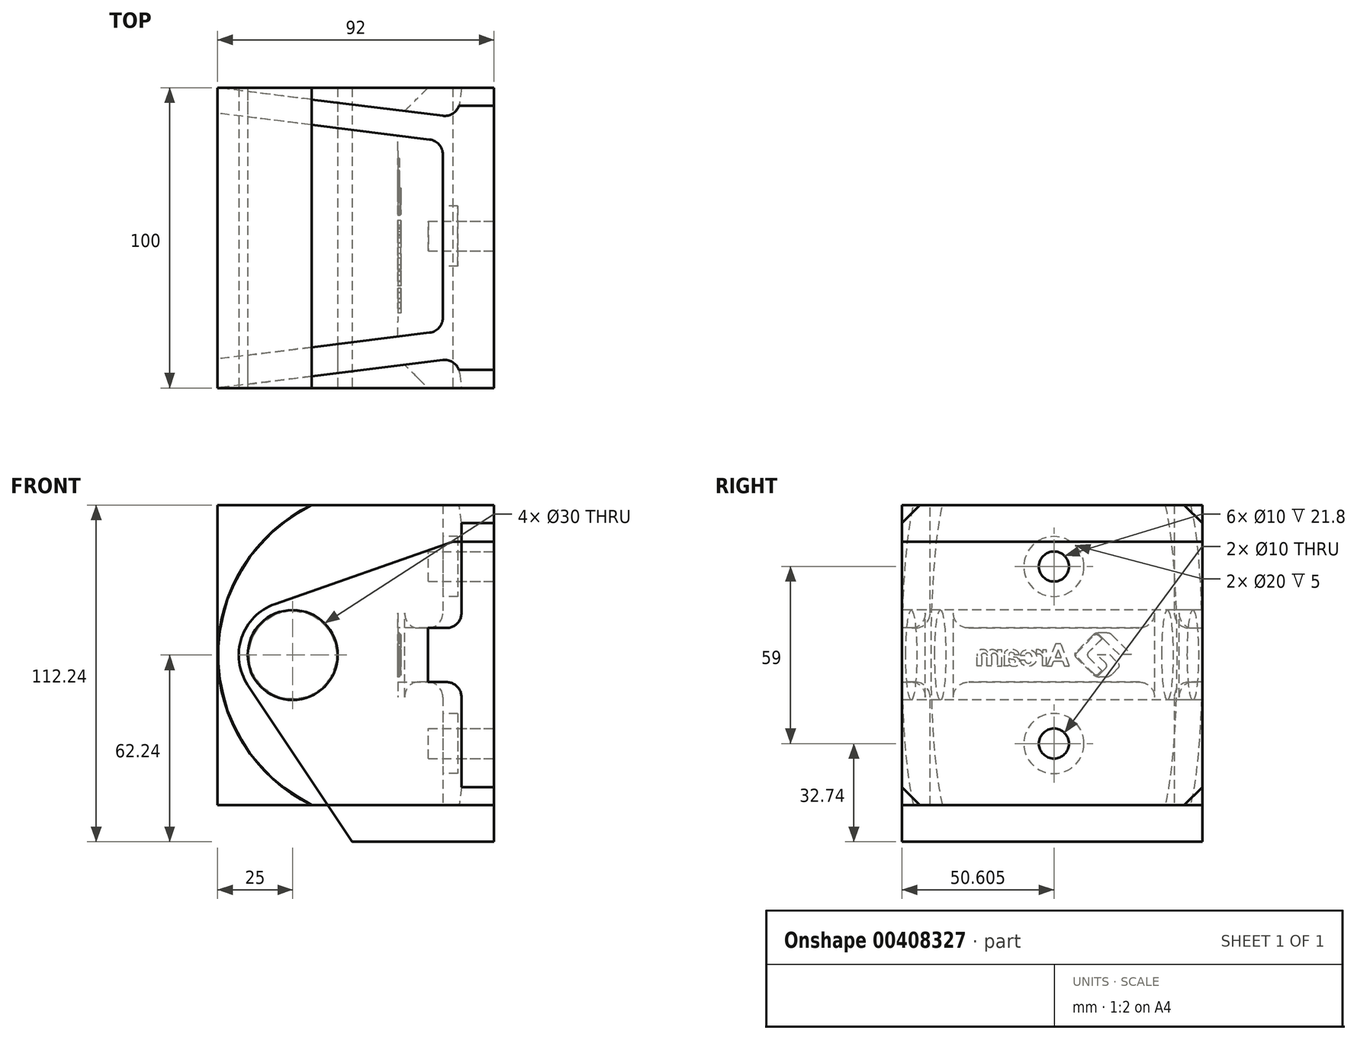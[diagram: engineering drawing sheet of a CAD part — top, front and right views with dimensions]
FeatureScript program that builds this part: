
annotation { "Feature Type Name" : "Feature", "Feature Type Description" : "" }
export const myFeature = defineFeature(function(context is Context, id is Id, definition is map)
    precondition{}
    {
        {
            assignVariable(context, id + "F0", {"name" : "length", "anyValue" : 100});
        }
        {
            assignVariable(context, id + "F1", {"name" : "thickness", "anyValue" : 12});
        }
        {
            var Q0;
            Q0=qCreatedBy(makeId("Top.planeOp"),FACE);
            var sketch = newSketch(context, id + "F2", { "sketchPlane" : qUnion([Q0])});
            skLineSegment(sketch, "E0", {"start": v(0, 0) * mm, "end": v(0, 100) * mm});
            skLineSegment(sketch, "E1", {"start": v(-92, 9.67) * mm, "end": v(-92, 0) * mm});
            skLineSegment(sketch, "E2", {"start": v(-92, 0) * mm, "end": v(-12.03, 9.92) * mm});
            skLineSegment(sketch, "E3", {"start": v(-12.03, 90.08) * mm, "end": v(-92, 100) * mm});
            skLineSegment(sketch, "E4", {"start": v(-92, 100) * mm, "end": v(-92, 91.54) * mm});
            skLineSegment(sketch, "E5", {"start": v(-92, 9.67) * mm, "end": v(-17, 18.98) * mm});
            skLineSegment(sketch, "E6", {"start": v(-17, 82.23) * mm, "end": v(-92, 91.54) * mm});
            skLineSegment(sketch, "E7", {"start": v(-10.8, 0) * mm, "end": v(0, 0) * mm});
            skLineSegment(sketch, "E8", {"start": v(-10.8, 100) * mm, "end": v(0, 100) * mm});
            skLineSegment(sketch, "E9", {"start": v(-12.03, 9.92) * mm, "end": v(-10.8, 0) * mm});
            skLineSegment(sketch, "E10", {"start": v(-17, 18.98) * mm, "end": v(-17, 82.23) * mm});
            skLineSegment(sketch, "E11", {"start": v(-12.03, 90.08) * mm, "end": v(-10.8, 100) * mm});
            skSolve(sketch);
        }
        {
            var Q0;
            Q0=makeQuery(id+"F2.imprint","IMPRINT",FACE,{"disambiguationData":[TD([[makeQuery(id+"F2.imprint","IMPRINT",EDGE,{"derivedFrom":sQuery(id+"F2.wireOp",EDGE,"E0")}),1.0]])]});
            extrude(context, id + "F3", {"entities" : qUnion([Q0]), "endBound" : BoundingType.SYMMETRIC, "depth" : 100 * mm});
        }
        {
            var Q0;
            Q0=qCreatedBy(makeId("Front.planeOp"),FACE);
            var sketch = newSketch(context, id + "F4", { "sketchPlane" : qUnion([Q0])});
            skLineSegment(sketch, "E12", {"start": v(-117, 60) * mm, "end": v(-117, -60) * mm});
            skLineSegment(sketch, "E13", {"start": v(-117, -60) * mm, "end": v(-47, -60) * mm});
            skLineSegment(sketch, "E14", {"start": v(-47, -60) * mm, "end": v(-107, 0) * mm});
            skLineSegment(sketch, "E15", {"start": v(-107, 0) * mm, "end": v(-47, 60) * mm});
            skLineSegment(sketch, "E16", {"start": v(-47, 60) * mm, "end": v(-117, 60) * mm});
            skArc(sketch, "E17", {"start": v(-12.03, 50) * mm, "mid": v(-92, 0) * mm, "end": v(-12.03, -50) * mm});
            skPoint(sketch, "E17.first.point", {"position": v(-12.03, 50) * mm});
            skPoint(sketch, "E17.second.point", {"position": v(-92, 0) * mm});
            skPoint(sketch, "E17.third.point", {"position": v(-12.03, -50) * mm});
            skLineSegment(sketch, "E18", {"start": v(-12.03, 50) * mm, "end": v(-12.03, -50) * mm});
            skArc(sketch, "E19.0", {"start": v(-12.03, 76.85) * mm, "mid": v(-117, 0) * mm, "end": v(-12.03, -76.85) * mm});
            skLineSegment(sketch, "E20", {"start": v(-12.03, 50) * mm, "end": v(-12.03, 76.85) * mm});
            skLineSegment(sketch, "E21", {"start": v(-12.03, -50) * mm, "end": v(-12.03, -76.85) * mm});
            skSolve(sketch);
        }
        {
            var Q0;
            {var subQ1=sQuery(id+"F4.wireOp",EDGE,"E14");var subQ6=sQuery(id+"F4.wireOp",EDGE,"E13");var subQ7=makeQuery(id+"F4.imprint","INTERSECT",VERTEX,{"derivedFrom":[subQ6,subQ1]});Q0=makeQuery(id+"F4.imprint","IMPRINT",FACE,{"disambiguationData":[TD([[makeQuery(id+"F4.imprint","IMPRINT",EDGE,{"disambiguationData":[TD([[subQ7,1.0]])],"derivedFrom":subQ6}),1.0]])]});}
            var Q1;
            {var subQ0=sQuery(id+"F4.wireOp",EDGE,"E15");var subQ1=sQuery(id+"F4.wireOp",EDGE,"E14");var subQ2=makeQuery(id+"F4.imprint","INTERSECT",VERTEX,{"derivedFrom":[subQ1,subQ0]});Q1=makeQuery(id+"F4.imprint","IMPRINT",FACE,{"disambiguationData":[TD([[makeQuery(id+"F4.imprint","IMPRINT",EDGE,{"disambiguationData":[TD([[subQ2,1.0]])],"derivedFrom":subQ1}),-1.0]])]});}
            var Q2;
            Q2 = qConstructionFilter(qBodyType(qCreatedBy(id + "F4" ,EDGE), BodyType.WIRE), ConstructionObject.NO);
            extrude(context, id + "F5", {"entities" : qUnion([Q0, Q1]), "operationType" : NewBodyOperationType.REMOVE, "surfaceEntities" : qUnion([Q2]), "oppositeDirection" : true, "depth" : 111.8 * mm});
        }
        {
            var Q0;
            Q0=qCreatedBy(makeId("Front.planeOp"),FACE);
            var sketch = newSketch(context, id + "F6", { "sketchPlane" : qUnion([Q0])});
            skCircle(sketch, "E22", {"center": v(-67, 0) * mm, "radius": 15 * mm});
            skSolve(sketch);
        }
        {
            var Q0;
            Q0 = qSketchRegion(id + "F6", true);
            var Q1;
            Q1=sQuery(id+"F6.wireOp",EDGE,"E22");
            extrude(context, id + "F7", {"entities" : qUnion([Q0]), "operationType" : NewBodyOperationType.REMOVE, "surfaceEntities" : qUnion([Q1]), "oppositeDirection" : true, "depth" : 108 * mm});
        }
        {
            var Q0;
            Q0=qCreatedBy(makeId("Front.planeOp"),FACE);
            var sketch = newSketch(context, id + "F8", { "sketchPlane" : qUnion([Q0])});
            skLineSegment(sketch, "E23.bottom", {"start": v(0, -9) * mm, "end": v(-32, -9) * mm});
            skLineSegment(sketch, "E23.top", {"start": v(0, 9) * mm, "end": v(-32, 9) * mm});
            skLineSegment(sketch, "E23.left", {"start": v(-32, 9) * mm, "end": v(-32, -9) * mm});
            skLineSegment(sketch, "E23.right", {"start": v(0, 9) * mm, "end": v(0, -9) * mm});
            skSolve(sketch);
        }
        {
            var Q0;
            Q0 = qSketchRegion(id + "F8", true);
            extrude(context, id + "F9", {"entities" : qUnion([Q0]), "operationType" : NewBodyOperationType.ADD, "oppositeDirection" : true, "depth" : (getVariable(context, 'length')) * mm});
        }
        {
            var Q0;
            Q0=makeQuery(id+"F3.opExtrude","CAP_EDGE",EDGE,{"disambiguationData":[OSD([sQuery(id+"F2.wireOp",EDGE,"vjMEqo8n-QfoI-5M5s-0d4p-3gr9z9UQkxS1")])],"isStart":true});
            var Q1;
            Q1=makeQuery(id+"F3.opExtrude","CAP_EDGE",EDGE,{"disambiguationData":[OSD([sQuery(id+"F2.wireOp",EDGE,"vjMEqo8n-QfoI-5M5s-0d4p-3gr9z9UQkxS1")])],"isStart":false});
            var Q2;
            Q2=makeQuery(id+"F3.opExtrude","CAP_EDGE",EDGE,{"disambiguationData":[OSD([sQuery(id+"F2.wireOp",EDGE,"uyNWYaNW-0dKr-tjX5-kQlW-Z3eX3tDSU0gN")])],"isStart":true});
            var Q3;
            Q3=makeQuery(id+"F3.opExtrude","CAP_EDGE",EDGE,{"disambiguationData":[OSD([sQuery(id+"F2.wireOp",EDGE,"uyNWYaNW-0dKr-tjX5-kQlW-Z3eX3tDSU0gN")])],"isStart":false});
            var Q4;
            Q4=makeQuery(id+"F3.opExtrude","CAP_EDGE",EDGE,{"disambiguationData":[OSD([sQuery(id+"F2.wireOp",EDGE,"E8")])],"isStart":false});
            var Q5;
            Q5=makeQuery(id+"F3.opExtrude","CAP_EDGE",EDGE,{"disambiguationData":[OSD([sQuery(id+"F2.wireOp",EDGE,"E8")])],"isStart":true});
            var Q6;
            Q6=makeQuery(id+"F3.opExtrude","CAP_EDGE",EDGE,{"disambiguationData":[OSD([sQuery(id+"F2.wireOp",EDGE,"E7")])],"isStart":true});
            var Q7;
            Q7=makeQuery(id+"F3.opExtrude","CAP_EDGE",EDGE,{"disambiguationData":[OSD([sQuery(id+"F2.wireOp",EDGE,"E7")])],"isStart":false});
            chamfer(context, id + "F10", {"entities" : qUnion([Q0, Q1, Q2, Q3, Q4, Q5, Q6, Q7]), "width" : 6 * mm, "tangentPropagation" : true});
        }
        {
            var Q0;
            Q0=qCreatedBy(makeId("Right.planeOp"),FACE);
            var sketch = newSketch(context, id + "F11", { "sketchPlane" : qUnion([Q0])});
            skCircle(sketch, "E24", {"center": v(50.6, 29.5) * mm, "radius": 5 * mm});
            skCircle(sketch, "E25.MirrorC", {"center": v(50.6, -29.5) * mm, "radius": 5 * mm});
            skLineSegment(sketch, "E26.direction1", {"start": v(50.6, 29.5) * mm, "end": v(19.52, 29.5) * mm, "construction": true});
            skLineSegment(sketch, "E27", {"start": v(82.23, 29.5) * mm, "end": v(18.98, 29.5) * mm});
            skLineSegment(sketch, "E28", {"start": v(50.6, 50) * mm, "end": v(50.6, 9) * mm});
            skSolve(sketch);
        }
        {
            var Q0;
            Q0 = qSketchRegion(id + "F11", true);
            extrude(context, id + "F12", {"entities" : qUnion([Q0]), "operationType" : NewBodyOperationType.REMOVE, "endBound" : BoundingType.UP_TO_NEXT, "oppositeDirection" : true, "depth" : (getVariable(context, 'thickness')) * mm});
        }
        {
            var Q0;
            {var subQ0=sQuery(id+"F2.wireOp",EDGE,"E10");Q0=makeQuery(id+"F9.boolean.opBoolean","SPLIT",FACE,{"disambiguationData":[TD([makeQuery(id+"F9.opExtrude","SWEPT_FACE",FACE,{"disambiguationData":[OSD([sQuery(id+"F8.wireOp",EDGE,"E23.bottom")])]})])],"derivedFrom":makeQuery(id+"F3.opExtrude","SWEPT_FACE",FACE,{"disambiguationData":[OSD([subQ0])]})});}
            cPlane(context, id + "F13", {"entities" : qUnion([Q0]), "cplaneType" : CPlaneType.OFFSET, "offset" : 0 * mm, "width" : 150 * mm, "height" : 150 * mm});
        }
        {
            var Q0;
            Q0=qCreatedBy(id+"F13.planeOp",FACE);
            var sketch = newSketch(context, id + "F14", { "sketchPlane" : qUnion([Q0])});
            skCircle(sketch, "E29.0", {"center": v(-50.6, 29.5) * mm, "radius": 10 * mm});
            skCircle(sketch, "E30.0", {"center": v(-50.6, -29.5) * mm, "radius": 10 * mm});
            skSolve(sketch);
        }
        {
            var Q0;
            Q0 = qSketchRegion(id + "F14", true);
            extrude(context, id + "F15", {"entities" : qUnion([Q0]), "operationType" : NewBodyOperationType.REMOVE, "oppositeDirection" : true, "depth" : 5 * mm});
        }
        {
            assignVariable(context, id + "F16", {"name" : "millradius", "anyValue" : 5});
        }
        {
            var Q0;
            Q0=makeQuery(id+"F9.boolean.opBoolean","INTERSECT",EDGE,{"derivedFrom":[makeQuery(id+"F3.opExtrude","SWEPT_FACE",FACE,{"disambiguationData":[OSD([sQuery(id+"F2.wireOp",EDGE,"E9")])]}),makeQuery(id+"F9.opExtrude","SWEPT_FACE",FACE,{"disambiguationData":[OSD([sQuery(id+"F8.wireOp",EDGE,"E23.top")])]})]});
            var Q1;
            Q1=makeQuery(id+"F9.boolean.opBoolean","INTERSECT",EDGE,{"derivedFrom":[makeQuery(id+"F3.opExtrude","SWEPT_FACE",FACE,{"disambiguationData":[OSD([sQuery(id+"F2.wireOp",EDGE,"E2")])]}),makeQuery(id+"F9.opExtrude","SWEPT_FACE",FACE,{"disambiguationData":[OSD([sQuery(id+"F8.wireOp",EDGE,"E23.top")])]})]});
            var Q2;
            {var subQ0=sQuery(id+"F2.wireOp",EDGE,"E9");var subQ1=sQuery(id+"F2.wireOp",EDGE,"E2");Q2=makeQuery(id+"F9.boolean.opBoolean","SPLIT",EDGE,{"disambiguationData":[TD([makeQuery(id+"F9.opExtrude","SWEPT_FACE",FACE,{"disambiguationData":[OSD([sQuery(id+"F8.wireOp",EDGE,"E23.top")])]})])],"derivedFrom":makeQuery(id+"F3.opExtrude","SWEPT_EDGE",EDGE,{"disambiguationData":[OSD([subQ1,subQ0])]})});}
            var Q3;
            Q3=makeQuery(id+"F9.boolean.opBoolean","INTERSECT",EDGE,{"derivedFrom":[makeQuery(id+"F3.opExtrude","SWEPT_FACE",FACE,{"disambiguationData":[OSD([sQuery(id+"F2.wireOp",EDGE,"E2")])]}),makeQuery(id+"F9.opExtrude","SWEPT_FACE",FACE,{"disambiguationData":[OSD([sQuery(id+"F8.wireOp",EDGE,"E23.bottom")])]})]});
            var Q4;
            Q4=makeQuery(id+"F9.boolean.opBoolean","INTERSECT",EDGE,{"derivedFrom":[makeQuery(id+"F3.opExtrude","SWEPT_FACE",FACE,{"disambiguationData":[OSD([sQuery(id+"F2.wireOp",EDGE,"E9")])]}),makeQuery(id+"F9.opExtrude","SWEPT_FACE",FACE,{"disambiguationData":[OSD([sQuery(id+"F8.wireOp",EDGE,"E23.bottom")])]})]});
            var Q5;
            {var subQ0=sQuery(id+"F2.wireOp",EDGE,"E9");var subQ1=sQuery(id+"F2.wireOp",EDGE,"E2");Q5=makeQuery(id+"F9.boolean.opBoolean","SPLIT",EDGE,{"disambiguationData":[TD([makeQuery(id+"F9.opExtrude","SWEPT_FACE",FACE,{"disambiguationData":[OSD([sQuery(id+"F8.wireOp",EDGE,"E23.bottom")])]})])],"derivedFrom":makeQuery(id+"F3.opExtrude","SWEPT_EDGE",EDGE,{"disambiguationData":[OSD([subQ1,subQ0])]})});}
            var Q6;
            {var subQ0=sQuery(id+"F2.wireOp",EDGE,"E10");var subQ1=sQuery(id+"F2.wireOp",EDGE,"E5");Q6=makeQuery(id+"F9.boolean.opBoolean","SPLIT",EDGE,{"disambiguationData":[TD([makeQuery(id+"F9.opExtrude","SWEPT_FACE",FACE,{"disambiguationData":[OSD([sQuery(id+"F8.wireOp",EDGE,"E23.top")])]})])],"derivedFrom":makeQuery(id+"F3.opExtrude","SWEPT_EDGE",EDGE,{"disambiguationData":[OSD([subQ1,subQ0])]})});}
            var Q7;
            Q7=makeQuery(id+"F9.boolean.opBoolean","INTERSECT",EDGE,{"derivedFrom":[makeQuery(id+"F3.opExtrude","SWEPT_FACE",FACE,{"disambiguationData":[OSD([sQuery(id+"F2.wireOp",EDGE,"E5")])]}),makeQuery(id+"F9.opExtrude","SWEPT_FACE",FACE,{"disambiguationData":[OSD([sQuery(id+"F8.wireOp",EDGE,"E23.top")])]})]});
            var Q8;
            Q8=makeQuery(id+"F9.boolean.opBoolean","INTERSECT",EDGE,{"derivedFrom":[makeQuery(id+"F3.opExtrude","SWEPT_FACE",FACE,{"disambiguationData":[OSD([sQuery(id+"F2.wireOp",EDGE,"E10")])]}),makeQuery(id+"F9.opExtrude","SWEPT_FACE",FACE,{"disambiguationData":[OSD([sQuery(id+"F8.wireOp",EDGE,"E23.top")])]})]});
            var Q9;
            Q9=makeQuery(id+"F9.boolean.opBoolean","INTERSECT",EDGE,{"derivedFrom":[makeQuery(id+"F3.opExtrude","SWEPT_FACE",FACE,{"disambiguationData":[OSD([sQuery(id+"F2.wireOp",EDGE,"E6")])]}),makeQuery(id+"F9.opExtrude","SWEPT_FACE",FACE,{"disambiguationData":[OSD([sQuery(id+"F8.wireOp",EDGE,"E23.top")])]})]});
            var Q10;
            {var subQ0=sQuery(id+"F2.wireOp",EDGE,"E10");var subQ1=sQuery(id+"F2.wireOp",EDGE,"E6");Q10=makeQuery(id+"F9.boolean.opBoolean","SPLIT",EDGE,{"disambiguationData":[TD([makeQuery(id+"F9.opExtrude","SWEPT_FACE",FACE,{"disambiguationData":[OSD([sQuery(id+"F8.wireOp",EDGE,"E23.top")])]})])],"derivedFrom":makeQuery(id+"F3.opExtrude","SWEPT_EDGE",EDGE,{"disambiguationData":[OSD([subQ1,subQ0])]})});}
            var Q11;
            {var subQ0=sQuery(id+"F2.wireOp",EDGE,"E10");var subQ1=sQuery(id+"F2.wireOp",EDGE,"E6");Q11=makeQuery(id+"F9.boolean.opBoolean","SPLIT",EDGE,{"disambiguationData":[TD([makeQuery(id+"F9.opExtrude","SWEPT_FACE",FACE,{"disambiguationData":[OSD([sQuery(id+"F8.wireOp",EDGE,"E23.bottom")])]})])],"derivedFrom":makeQuery(id+"F3.opExtrude","SWEPT_EDGE",EDGE,{"disambiguationData":[OSD([subQ1,subQ0])]})});}
            var Q12;
            Q12=makeQuery(id+"F9.boolean.opBoolean","INTERSECT",EDGE,{"derivedFrom":[makeQuery(id+"F3.opExtrude","SWEPT_FACE",FACE,{"disambiguationData":[OSD([sQuery(id+"F2.wireOp",EDGE,"E6")])]}),makeQuery(id+"F9.opExtrude","SWEPT_FACE",FACE,{"disambiguationData":[OSD([sQuery(id+"F8.wireOp",EDGE,"E23.bottom")])]})]});
            var Q13;
            Q13=makeQuery(id+"F9.boolean.opBoolean","INTERSECT",EDGE,{"derivedFrom":[makeQuery(id+"F3.opExtrude","SWEPT_FACE",FACE,{"disambiguationData":[OSD([sQuery(id+"F2.wireOp",EDGE,"E10")])]}),makeQuery(id+"F9.opExtrude","SWEPT_FACE",FACE,{"disambiguationData":[OSD([sQuery(id+"F8.wireOp",EDGE,"E23.bottom")])]})]});
            var Q14;
            Q14=makeQuery(id+"F9.boolean.opBoolean","INTERSECT",EDGE,{"derivedFrom":[makeQuery(id+"F3.opExtrude","SWEPT_FACE",FACE,{"disambiguationData":[OSD([sQuery(id+"F2.wireOp",EDGE,"E5")])]}),makeQuery(id+"F9.opExtrude","SWEPT_FACE",FACE,{"disambiguationData":[OSD([sQuery(id+"F8.wireOp",EDGE,"E23.bottom")])]})]});
            var Q15;
            {var subQ0=sQuery(id+"F2.wireOp",EDGE,"E10");var subQ1=sQuery(id+"F2.wireOp",EDGE,"E5");Q15=makeQuery(id+"F9.boolean.opBoolean","SPLIT",EDGE,{"disambiguationData":[TD([makeQuery(id+"F9.opExtrude","SWEPT_FACE",FACE,{"disambiguationData":[OSD([sQuery(id+"F8.wireOp",EDGE,"E23.bottom")])]})])],"derivedFrom":makeQuery(id+"F3.opExtrude","SWEPT_EDGE",EDGE,{"disambiguationData":[OSD([subQ1,subQ0])]})});}
            var Q16;
            Q16=makeQuery(id+"F9.boolean.opBoolean","INTERSECT",EDGE,{"derivedFrom":[makeQuery(id+"F3.opExtrude","SWEPT_FACE",FACE,{"disambiguationData":[OSD([sQuery(id+"F2.wireOp",EDGE,"E3")])]}),makeQuery(id+"F9.opExtrude","SWEPT_FACE",FACE,{"disambiguationData":[OSD([sQuery(id+"F8.wireOp",EDGE,"E23.bottom")])]})]});
            var Q17;
            Q17=makeQuery(id+"F9.boolean.opBoolean","INTERSECT",EDGE,{"derivedFrom":[makeQuery(id+"F3.opExtrude","SWEPT_FACE",FACE,{"disambiguationData":[OSD([sQuery(id+"F2.wireOp",EDGE,"E11")])]}),makeQuery(id+"F9.opExtrude","SWEPT_FACE",FACE,{"disambiguationData":[OSD([sQuery(id+"F8.wireOp",EDGE,"E23.bottom")])]})]});
            var Q18;
            {var subQ0=sQuery(id+"F2.wireOp",EDGE,"E11");var subQ1=sQuery(id+"F2.wireOp",EDGE,"E3");Q18=makeQuery(id+"F9.boolean.opBoolean","SPLIT",EDGE,{"disambiguationData":[TD([makeQuery(id+"F9.opExtrude","SWEPT_FACE",FACE,{"disambiguationData":[OSD([sQuery(id+"F8.wireOp",EDGE,"E23.bottom")])]})])],"derivedFrom":makeQuery(id+"F3.opExtrude","SWEPT_EDGE",EDGE,{"disambiguationData":[OSD([subQ1,subQ0])]})});}
            var Q19;
            Q19=makeQuery(id+"F9.boolean.opBoolean","INTERSECT",EDGE,{"derivedFrom":[makeQuery(id+"F3.opExtrude","SWEPT_FACE",FACE,{"disambiguationData":[OSD([sQuery(id+"F2.wireOp",EDGE,"E3")])]}),makeQuery(id+"F9.opExtrude","SWEPT_FACE",FACE,{"disambiguationData":[OSD([sQuery(id+"F8.wireOp",EDGE,"E23.top")])]})]});
            var Q20;
            Q20=makeQuery(id+"F9.boolean.opBoolean","INTERSECT",EDGE,{"derivedFrom":[makeQuery(id+"F3.opExtrude","SWEPT_FACE",FACE,{"disambiguationData":[OSD([sQuery(id+"F2.wireOp",EDGE,"E11")])]}),makeQuery(id+"F9.opExtrude","SWEPT_FACE",FACE,{"disambiguationData":[OSD([sQuery(id+"F8.wireOp",EDGE,"E23.top")])]})]});
            var Q21;
            {var subQ0=sQuery(id+"F2.wireOp",EDGE,"E11");var subQ1=sQuery(id+"F2.wireOp",EDGE,"E3");Q21=makeQuery(id+"F9.boolean.opBoolean","SPLIT",EDGE,{"disambiguationData":[TD([makeQuery(id+"F9.opExtrude","SWEPT_FACE",FACE,{"disambiguationData":[OSD([sQuery(id+"F8.wireOp",EDGE,"E23.top")])]})])],"derivedFrom":makeQuery(id+"F3.opExtrude","SWEPT_EDGE",EDGE,{"disambiguationData":[OSD([subQ1,subQ0])]})});}
            fillet(context, id + "F17", {"entities" : qUnion([Q0, Q1, Q2, Q3, Q4, Q5, Q6, Q7, Q8, Q9, Q10, Q11, Q12, Q13, Q14, Q15, Q16, Q17, Q18, Q19, Q20, Q21]), "radius" : (getVariable(context, 'millradius')) * mm, "tangentPropagation" : true, "allowEdgeOverflow" : false});
        }
        {
            var Q0;
            Q0=makeQuery(id+"F9.opExtrude","CAP_EDGE",EDGE,{"disambiguationData":[OSD([sQuery(id+"F8.wireOp",EDGE,"E23.left")])],"isStart":true});
            var Q1;
            Q1=makeQuery(id+"F9.opExtrude","CAP_EDGE",EDGE,{"disambiguationData":[OSD([sQuery(id+"F8.wireOp",EDGE,"E23.left")])],"isStart":false});
            chamfer(context, id + "F18", {"entities" : qUnion([Q0, Q1]), "width" : 10 * mm, "tangentPropagation" : true});
        }
        {
            var Q0;
            Q0=qCreatedBy(makeId("Top.planeOp"),FACE);
            var sketch = newSketch(context, id + "F19", { "sketchPlane" : qUnion([Q0])});
            skLineSegment(sketch, "E31.bottom", {"start": v(0, 0) * mm, "end": v(-92, 0) * mm});
            skLineSegment(sketch, "E31.top", {"start": v(0, 100) * mm, "end": v(-92, 100) * mm});
            skLineSegment(sketch, "E31.left", {"start": v(0, 0) * mm, "end": v(0, 100) * mm});
            skLineSegment(sketch, "E31.right", {"start": v(-92, 0) * mm, "end": v(-92, 100) * mm});
            skSolve(sketch);
        }
        {
            var Q0;
            Q0 = qSketchRegion(id + "F19", true);
            extrude(context, id + "F20", {"entities" : qUnion([Q0]), "endBound" : BoundingType.SYMMETRIC, "depth" : (getVariable(context, 'length')) * mm});
        }
        {
            var Q0;
            Q0=makeQuery(id+"F9.boolean.opBoolean","MERGE",FACE,{"derivedFrom":[makeQuery(id+"F3.opExtrude","SWEPT_FACE",FACE,{"disambiguationData":[OSD([sQuery(id+"F2.wireOp",EDGE,"E7")])]}),makeQuery(id+"F9.opExtrude","CAP_FACE",FACE,{"disambiguationData":[OSD([sQuery(id+"F8.wireOp",EDGE,"E23.bottom"),sQuery(id+"F8.wireOp",EDGE,"E23.top"),sQuery(id+"F8.wireOp",EDGE,"E23.left"),sQuery(id+"F8.wireOp",EDGE,"E23.right")])],"isStart":true})]});
            cPlane(context, id + "F21", {"entities" : qUnion([Q0]), "cplaneType" : CPlaneType.OFFSET, "offset" : 0 * mm, "width" : 150 * mm, "height" : 150 * mm});
        }
        {
            var Q0;
            Q0=qCreatedBy(id+"F21.planeOp",FACE);
            var sketch = newSketch(context, id + "F22", { "sketchPlane" : qUnion([Q0])});
            skLineSegment(sketch, "E32.0", {"start": v(-60.74, -50) * mm, "end": v(-17, -50) * mm});
            skLineSegment(sketch, "E32.1", {"start": v(-11.66, -50) * mm, "end": v(-17, -50) * mm});
            skArc(sketch, "E32.2", {"start": v(-60.74, -50) * mm, "mid": v(-92, 0) * mm, "end": v(-60.74, 50) * mm});
            skLineSegment(sketch, "E32.3", {"start": v(0, -50) * mm, "end": v(-11.66, -50) * mm});
            skLineSegment(sketch, "E32.4", {"start": v(0, -44) * mm, "end": v(0, -50) * mm});
            skLineSegment(sketch, "E32.5", {"start": v(0, 44) * mm, "end": v(0, -44) * mm});
            skLineSegment(sketch, "E32.6", {"start": v(-60.74, 50) * mm, "end": v(-17, 50) * mm});
            skLineSegment(sketch, "E32.7", {"start": v(-17, 50) * mm, "end": v(-11.66, 50) * mm});
            skLineSegment(sketch, "E32.8", {"start": v(-11.66, 50) * mm, "end": v(0, 50) * mm});
            skLineSegment(sketch, "E32.9", {"start": v(0, 50) * mm, "end": v(0, 44) * mm});
            skCircle(sketch, "E33.0", {"center": v(-67, 0) * mm, "radius": 15 * mm});
            skSolve(sketch);
        }
        {
            var Q0;
            Q0 = qSketchRegion(id + "F22", true);
            extrude(context, id + "F23", {"entities" : qUnion([Q0]), "oppositeDirection" : true, "depth" : (getVariable(context, 'length')) * mm});
        }
        {
            var Q0;
            Q0=qCreatedBy(id+"F21.planeOp",FACE);
            var sketch = newSketch(context, id + "F24", { "sketchPlane" : qUnion([Q0])});
            skLineSegment(sketch, "E34", {"start": v(0, 37.76) * mm, "end": v(0, -62.24) * mm});
            skArc(sketch, "E35", {"start": v(-72.96, 16.99) * mm, "mid": v(-84.07, 5.72) * mm, "end": v(-82, -9.96) * mm});
            skLineSegment(sketch, "E36", {"start": v(0, 37.76) * mm, "end": v(-13.73, 37.76) * mm});
            skLineSegment(sketch, "E37", {"start": v(-13.73, 37.76) * mm, "end": v(-72.96, 16.99) * mm});
            skLineSegment(sketch, "E38", {"start": v(0, -62.24) * mm, "end": v(-47.26, -62.24) * mm});
            skLineSegment(sketch, "E39", {"start": v(-47.26, -62.24) * mm, "end": v(-82, -9.96) * mm});
            skCircle(sketch, "E40", {"center": v(-67, 0) * mm, "radius": 15 * mm});
            skSolve(sketch);
        }
        {
            var Q0;
            {var subQ0=sQuery(id+"F24.wireOp",EDGE,"E37");Q0=makeQuery(id+"F24.imprint","IMPRINT",FACE,{"disambiguationData":[TD([[makeQuery(id+"F24.imprint","IMPRINT",EDGE,{"derivedFrom":subQ0}),1.0]])]});}
            var Q1;
            {var subQ0=sQuery(id+"F24.wireOp",EDGE,"E39");Q1=makeQuery(id+"F24.imprint","IMPRINT",FACE,{"disambiguationData":[TD([[makeQuery(id+"F24.imprint","IMPRINT",EDGE,{"derivedFrom":subQ0}),-1.0]])]});}
            extrude(context, id + "F25", {"entities" : qUnion([Q0, Q1]), "oppositeDirection" : true, "depth" : (getVariable(context, 'length')) * mm});
        }
        {
            var Q0;
            Q0=makeQuery(id+"F3.opExtrude","SWEPT_FACE",FACE,{"disambiguationData":[OSD([sQuery(id+"F2.wireOp",EDGE,"E0")])]});
            cPlane(context, id + "F26", {"entities" : qUnion([Q0]), "cplaneType" : CPlaneType.OFFSET, "offset" : 0 * mm, "width" : 150 * mm, "height" : 150 * mm});
        }
        {
            var Q0;
            Q0=qCreatedBy(id+"F26.planeOp",FACE);
            var sketch = newSketch(context, id + "F27", { "sketchPlane" : qUnion([Q0])});
            skCircle(sketch, "E41", {"center": v(50.6, 29.5) * mm, "radius": 5 * mm});
            skCircle(sketch, "E42", {"center": v(50.6, -29.5) * mm, "radius": 5 * mm});
            skSolve(sketch);
        }
        {
            var Q0;
            Q0 = qSketchRegion(id + "F27", true);
            extrude(context, id + "F28", {"entities" : qUnion([Q0]), "operationType" : NewBodyOperationType.REMOVE, "oppositeDirection" : true, "depth" : 21.8 * mm});
        }
        {
            var Q0;
            Q0=makeQuery(id+"F9.boolean.opBoolean","SPLIT",FACE,{"disambiguationData":[TD([makeQuery(id+"F3.opExtrude","SWEPT_FACE",FACE,{"disambiguationData":[OSD([sQuery(id+"F2.wireOp",EDGE,"E5")])]})])],"derivedFrom":makeQuery(id+"F9.opExtrude","SWEPT_FACE",FACE,{"disambiguationData":[OSD([sQuery(id+"F8.wireOp",EDGE,"E23.left")])]})});
            var sketch = newSketch(context, id + "F29", { "sketchPlane" : qUnion([Q0])});
            skLineSegment(sketch, "E43", {"start": v(-76.5, 0.1) * mm, "end": v(-72.33, 0.1) * mm});
            skLineSegment(sketch, "E44", {"start": v(-72.33, 0.1) * mm, "end": v(-66.8, 5.63) * mm});
            skLineSegment(sketch, "E45", {"start": v(-66.8, 5.63) * mm, "end": v(-61.99, 0.81) * mm});
            skLineSegment(sketch, "E46", {"start": v(-61.99, -0.6) * mm, "end": v(-66.8, -5.4) * mm});
            skLineSegment(sketch, "E47", {"start": v(-66.8, -5.4) * mm, "end": v(-67.88, -4.33) * mm});
            skLineSegment(sketch, "E48", {"start": v(-67.88, -2.78) * mm, "end": v(-64.99, 0.1) * mm});
            skLineSegment(sketch, "E49", {"start": v(-64.99, 0.1) * mm, "end": v(-69.16, 0.1) * mm});
            skLineSegment(sketch, "E50", {"start": v(-69.16, 0.1) * mm, "end": v(-72.13, -2.86) * mm});
            skLineSegment(sketch, "E51", {"start": v(-72.18, -4.2) * mm, "end": v(-69.93, -6.44) * mm});
            skLineSegment(sketch, "E52", {"start": v(-63.77, -6.56) * mm, "end": v(-57.81, -0.6) * mm});
            skLineSegment(sketch, "E53", {"start": v(-57.81, 0.81) * mm, "end": v(-63.85, 6.85) * mm});
            skLineSegment(sketch, "E54", {"start": v(-69.77, 6.85) * mm, "end": v(-76.5, 0.1) * mm});
            skLineSegment(sketch, "E55", {"start": v(-68.27, 7.35) * mm, "end": v(-65.35, 7.35) * mm});
            skLineSegment(sketch, "E56", {"start": v(-67.78, -7.31) * mm, "end": v(-65.77, -7.31) * mm});
            skArc(sketch, "E57", {"start": v(-72.13, -2.86) * mm, "mid": v(-72.38, -3.52) * mm, "end": v(-72.18, -4.2) * mm});
            skArc(sketch, "E58", {"start": v(-67.88, -2.78) * mm, "mid": v(-68.2, -3.56) * mm, "end": v(-67.88, -4.33) * mm});
            skLineSegment(sketch, "E59", {"start": v(-66.8, -5.4) * mm, "end": v(-65.65, -6.56) * mm});
            skArc(sketch, "E60", {"start": v(-65.65, -6.56) * mm, "mid": v(-64.7, -6.95) * mm, "end": v(-63.77, -6.56) * mm});
            skArc(sketch, "E61", {"start": v(-66.13, -7.31) * mm, "mid": v(-65.11, -7.22) * mm, "end": v(-64.17, -6.83) * mm});
            skArc(sketch, "E62", {"start": v(-69.93, -6.44) * mm, "mid": v(-68.78, -7.12) * mm, "end": v(-67.46, -7.31) * mm});
            skArc(sketch, "E63", {"start": v(-61.99, -0.6) * mm, "mid": v(-61.76, 0.1) * mm, "end": v(-61.99, 0.81) * mm});
            skPoint(sketch, "E64.orphan", {"position": v(-57.81, 0.81) * mm});
            skPoint(sketch, "E65.start.orphan", {"position": v(-57.81, -0.6) * mm});
            skArc(sketch, "E66", {"start": v(-57.81, -0.6) * mm, "mid": v(-57.52, 0.1) * mm, "end": v(-57.81, 0.81) * mm});
            skArc(sketch, "E67", {"start": v(-63.85, 6.85) * mm, "mid": v(-64.56, 7.22) * mm, "end": v(-65.35, 7.35) * mm});
            skArc(sketch, "E68", {"start": v(-68.27, 7.35) * mm, "mid": v(-69.06, 7.22) * mm, "end": v(-69.77, 6.85) * mm});
            skLineSegment(sketch, "E69", {"start": v(-55.77, -3.69) * mm, "end": v(-52.93, 3.7) * mm});
            skLineSegment(sketch, "E70", {"start": v(-52.93, 3.7) * mm, "end": v(-51.13, 3.7) * mm});
            skLineSegment(sketch, "E71", {"start": v(-51.13, 3.7) * mm, "end": v(-48.29, -3.69) * mm});
            skLineSegment(sketch, "E72", {"start": v(-48.29, -3.69) * mm, "end": v(-49.95, -3.69) * mm});
            skLineSegment(sketch, "E73", {"start": v(-49.95, -3.69) * mm, "end": v(-50.59, -2.02) * mm});
            skLineSegment(sketch, "E74", {"start": v(-50.59, -2.02) * mm, "end": v(-53.48, -2.02) * mm});
            skLineSegment(sketch, "E75", {"start": v(-53.48, -2.02) * mm, "end": v(-54.11, -3.69) * mm});
            skLineSegment(sketch, "E76", {"start": v(-54.11, -3.69) * mm, "end": v(-55.77, -3.69) * mm});
            skLineSegment(sketch, "E77", {"start": v(-53.04, -0.89) * mm, "end": v(-52.03, 1.74) * mm});
            skLineSegment(sketch, "E78", {"start": v(-52.03, 1.74) * mm, "end": v(-51.02, -0.89) * mm});
            skLineSegment(sketch, "E79", {"start": v(-51.02, -0.89) * mm, "end": v(-53.04, -0.89) * mm});
            skLineSegment(sketch, "E80", {"start": v(-48.18, -3.7) * mm, "end": v(-48.18, 1.68) * mm});
            skLineSegment(sketch, "E81", {"start": v(-48.18, 1.68) * mm, "end": v(-46.8, 1.68) * mm});
            skLineSegment(sketch, "E82", {"start": v(-46.8, 1.68) * mm, "end": v(-46.8, 0.64) * mm});
            skLineSegment(sketch, "E83", {"start": v(-44.74, 1.78) * mm, "end": v(-44.74, 0.42) * mm});
            skLineSegment(sketch, "E84", {"start": v(-48.18, -3.7) * mm, "end": v(-46.8, -3.7) * mm});
            skLineSegment(sketch, "E85", {"start": v(-46.8, -3.7) * mm, "end": v(-46.8, -1.02) * mm});
            skFitSpline(sketch, "E86", {"points": [v(-46.8, 0.64) * mm, v(-46.6, 1.03) * mm, v(-46.08, 1.53) * mm, v(-45.5, 1.8) * mm, v(-45.09, 1.84) * mm, v(-44.74, 1.78) * mm], "startDerivative": vector(0.85, 2.06) * mm, "endDerivative": vector(2.01, -0.5) * mm});
            skFitSpline(sketch, "E87", {"points": [v(-44.74, 0.42) * mm, v(-45.5, 0.46) * mm, v(-46.2, 0.19) * mm, v(-46.68, -0.46) * mm, v(-46.8, -1.02) * mm], "startDerivative": vector(-2.98, 0.4) * mm, "endDerivative": vector(-0.32, -2.43) * mm});
            skLineSegment(sketch, "E88", {"start": v(-40.95, -0.18) * mm, "end": v(-39.5, -0.18) * mm});
            skLineSegment(sketch, "E89", {"start": v(-39.48, -1.6) * mm, "end": v(-40.9, -1.6) * mm});
            skFitSpline(sketch, "E90", {"points": [v(-39.5, -0.18) * mm, v(-39.7, 0.67) * mm, v(-40.56, 1.5) * mm, v(-41.95, 1.84) * mm, v(-43.27, 1.57) * mm, v(-44.3, 0.76) * mm, v(-44.76, -0.4) * mm, v(-44.7, -1.83) * mm, v(-44.1, -3) * mm, v(-42.84, -3.72) * mm, v(-41.4, -3.77) * mm, v(-40.05, -3.05) * mm, v(-39.69, -2.4) * mm, v(-39.48, -1.6) * mm], "startDerivative": vector(-1.29, 13.4) * mm, "endDerivative": vector(3.13, 13.27) * mm});
            skFitSpline(sketch, "E91", {"points": [v(-40.9, -1.6) * mm, v(-40.96, -1.96) * mm, v(-41.34, -2.53) * mm, v(-42.1, -2.72) * mm, v(-42.79, -2.5) * mm, v(-43.2, -1.76) * mm, v(-43.3, -0.91) * mm, v(-43.15, -0.08) * mm, v(-42.66, 0.5) * mm, v(-42.09, 0.7) * mm, v(-41.7, 0.68) * mm, v(-41.21, 0.44) * mm, v(-40.95, -0.18) * mm], "startDerivative": vector(-0.32, -5.47) * mm, "endDerivative": vector(2.15, -8.36) * mm});
            skFitSpline(sketch, "E92", {"points": [v(-37.5, 0.04) * mm, v(-37.4, 0.42) * mm, v(-37.14, 0.72) * mm, v(-36.69, 0.84) * mm, v(-36.12, 0.85) * mm, v(-35.6, 0.42) * mm, v(-35.6, -0.1) * mm, v(-35.9, -0.38) * mm, v(-37.52, -0.61) * mm, v(-38.2, -0.8) * mm, v(-38.57, -1.01) * mm, v(-38.86, -1.22) * mm, v(-39.11, -1.94) * mm, v(-39.11, -2.54) * mm, v(-39, -3) * mm, v(-38.56, -3.51) * mm, v(-37.34, -3.84) * mm, v(-36.23, -3.63) * mm, v(-35.52, -3.23) * mm], "startDerivative": vector(1.58, 8.96) * mm, "endDerivative": vector(10.57, 7.04) * mm});
            skFitSpline(sketch, "E93", {"points": [v(-38.95, 0.04) * mm, v(-38.97, 0.34) * mm, v(-38.68, 0.93) * mm, v(-38.13, 1.45) * mm, v(-37.32, 1.77) * mm, v(-36.25, 1.87) * mm, v(-35.5, 1.78) * mm, v(-34.73, 1.52) * mm, v(-34.17, 0.89) * mm, v(-34.11, 0.46) * mm], "startDerivative": vector(-0.74, 3.8) * mm, "endDerivative": vector(0, -4.72) * mm});
            skFitSpline(sketch, "E94", {"points": [v(-35.58, -1.07) * mm, v(-35.78, -1.19) * mm, v(-36.66, -1.36) * mm, v(-37.3, -1.52) * mm, v(-37.61, -1.85) * mm, v(-37.65, -2.24) * mm, v(-37.53, -2.58) * mm, v(-37.25, -2.77) * mm, v(-36.23, -2.78) * mm, v(-35.84, -2.44) * mm, v(-35.58, -2.06) * mm], "startDerivative": vector(-2.22, -1.8) * mm, "endDerivative": vector(2.77, 4) * mm});
            skLineSegment(sketch, "E95", {"start": v(-38.95, 0.04) * mm, "end": v(-37.5, 0.04) * mm});
            skLineSegment(sketch, "E96", {"start": v(-35.58, -1.07) * mm, "end": v(-35.58, -2.06) * mm});
            skLineSegment(sketch, "E97", {"start": v(-35.52, -3.23) * mm, "end": v(-35.41, -3.68) * mm});
            skLineSegment(sketch, "E98", {"start": v(-35.41, -3.68) * mm, "end": v(-33.92, -3.68) * mm});
            skLineSegment(sketch, "E99", {"start": v(-33.92, -3.68) * mm, "end": v(-34.11, -3.13) * mm});
            skLineSegment(sketch, "E100", {"start": v(-34.11, -3.13) * mm, "end": v(-34.11, 0.46) * mm});
            skLineSegment(sketch, "E101", {"start": v(-31.72, -0.29) * mm, "end": v(-31.72, -3.66) * mm});
            skLineSegment(sketch, "E102", {"start": v(-31.72, -3.66) * mm, "end": v(-33.22, -3.66) * mm});
            skLineSegment(sketch, "E103", {"start": v(-33.22, -3.66) * mm, "end": v(-33.22, 1.66) * mm});
            skLineSegment(sketch, "E104", {"start": v(-33.22, 1.66) * mm, "end": v(-31.8, 1.66) * mm});
            skLineSegment(sketch, "E105", {"start": v(-31.8, 1.66) * mm, "end": v(-31.8, 0.96) * mm});
            skLineSegment(sketch, "E106", {"start": v(-29.83, -0.29) * mm, "end": v(-29.83, -3.66) * mm});
            skLineSegment(sketch, "E107", {"start": v(-29.83, -3.66) * mm, "end": v(-28.35, -3.66) * mm});
            skLineSegment(sketch, "E108", {"start": v(-28.35, -3.66) * mm, "end": v(-28.35, -0.29) * mm});
            skLineSegment(sketch, "E109", {"start": v(-26.5, -0.29) * mm, "end": v(-26.5, -3.66) * mm});
            skLineSegment(sketch, "E110", {"start": v(-26.5, -3.66) * mm, "end": v(-25, -3.66) * mm});
            skLineSegment(sketch, "E111", {"start": v(-25, -3.66) * mm, "end": v(-25, -0.29) * mm});
            skFitSpline(sketch, "E112", {"points": [v(-31.8, 0.96) * mm, v(-31.62, 1.19) * mm, v(-31.26, 1.52) * mm, v(-30.37, 1.82) * mm, v(-29.7, 1.8) * mm, v(-29.1, 1.55) * mm, v(-28.55, 0.96) * mm], "startDerivative": vector(1.45, 1.9) * mm, "endDerivative": vector(2.73, -3.47) * mm});
            skFitSpline(sketch, "E113", {"points": [v(-28.55, 0.96) * mm, v(-28.23, 1.34) * mm, v(-27.63, 1.74) * mm, v(-26.85, 1.85) * mm, v(-26, 1.7) * mm, v(-25.36, 1.24) * mm, v(-25.1, 0.72) * mm, v(-25, -0.29) * mm], "startDerivative": vector(2.43, 3.18) * mm, "endDerivative": vector(0.28, -6.58) * mm});
            skFitSpline(sketch, "E114", {"points": [v(-26.5, -0.29) * mm, v(-26.5, 0.04) * mm, v(-26.7, 0.4) * mm, v(-27.02, 0.64) * mm, v(-27.68, 0.64) * mm, v(-28.1, 0.36) * mm, v(-28.27, 0.1) * mm, v(-28.35, -0.29) * mm], "startDerivative": vector(0.34, 2.6) * mm, "endDerivative": vector(-0.36, -2.94) * mm});
            skFitSpline(sketch, "E115", {"points": [v(-29.83, -0.29) * mm, v(-29.83, -0.01) * mm, v(-30.04, 0.37) * mm, v(-30.37, 0.63) * mm, v(-30.93, 0.61) * mm, v(-31.32, 0.42) * mm, v(-31.58, 0.1) * mm, v(-31.72, -0.29) * mm], "startDerivative": vector(0.3, 2.27) * mm, "endDerivative": vector(-0.75, -2.85) * mm});
            skPoint(sketch, "E116.orphan", {"position": v(-66.8, 9.8) * mm});
            skPoint(sketch, "E117.orphan", {"position": v(-69.27, 7.35) * mm});
            skPoint(sketch, "E118.orphan", {"position": v(-64.35, 7.35) * mm});
            skPoint(sketch, "E119.orphan", {"position": v(-69.06, -7.31) * mm});
            skPoint(sketch, "E120.orphan", {"position": v(-64.53, -7.31) * mm});
            skPoint(sketch, "E121.orphan", {"position": v(-57.1, 0.1) * mm});
            skLineSegment(sketch, "E122", {"start": v(-66.8, 5.63) * mm, "end": v(-65.9, 6.54) * mm});
            skArc(sketch, "E123", {"start": v(-63.85, 6.85) * mm, "mid": v(-64.92, 7.03) * mm, "end": v(-65.9, 6.54) * mm});
            skSolve(sketch);
        }
        {
            var Q0;
            Q0=makeQuery(id+"F29.imprint","IMPRINT",FACE,{"disambiguationData":[TD([[makeQuery(id+"F29.imprint","IMPRINT",EDGE,{"derivedFrom":sQuery(id+"F29.wireOp",EDGE,"E45")}),1.0]])]});
            extrude(context, id + "F30", {"entities" : qUnion([Q0]), "operationType" : NewBodyOperationType.REMOVE, "oppositeDirection" : true, "depth" : 1 * mm});
        }
        {
            var Q0;
            Q0=makeQuery(id+"F29.imprint","IMPRINT",FACE,{"disambiguationData":[TD([[makeQuery(id+"F29.imprint","IMPRINT",EDGE,{"derivedFrom":sQuery(id+"F29.wireOp",EDGE,"E43")}),1.0]])]});
            var Q1;
            Q1=makeQuery(id+"F29.imprint","IMPRINT",FACE,{"disambiguationData":[TD([[makeQuery(id+"F29.imprint","IMPRINT",EDGE,{"derivedFrom":sQuery(id+"F29.wireOp",EDGE,"E47")}),1.0]])]});
            extrude(context, id + "F31", {"entities" : qUnion([Q0, Q1]), "operationType" : NewBodyOperationType.REMOVE, "oppositeDirection" : true, "depth" : 0.5 * mm});
        }
        {
            var Q0;
            Q0=makeQuery(id+"F29.imprint","IMPRINT",FACE,{"disambiguationData":[TD([[makeQuery(id+"F29.imprint","IMPRINT",EDGE,{"derivedFrom":sQuery(id+"F29.wireOp",EDGE,"E69")}),-1.0]])]});
            var Q1;
            Q1=makeQuery(id+"F29.imprint","IMPRINT",FACE,{"disambiguationData":[TD([[makeQuery(id+"F29.imprint","IMPRINT",EDGE,{"derivedFrom":sQuery(id+"F29.wireOp",EDGE,"E80")}),-1.0]])]});
            var Q2;
            Q2=makeQuery(id+"F29.imprint","IMPRINT",FACE,{"disambiguationData":[TD([[makeQuery(id+"F29.imprint","IMPRINT",EDGE,{"derivedFrom":sQuery(id+"F29.wireOp",EDGE,"E88")}),1.0]])]});
            var Q3;
            Q3=makeQuery(id+"F29.imprint","IMPRINT",FACE,{"disambiguationData":[TD([[makeQuery(id+"F29.imprint","IMPRINT",EDGE,{"derivedFrom":sQuery(id+"F29.wireOp",EDGE,"E92")}),1.0]])]});
            var Q4;
            Q4=makeQuery(id+"F29.imprint","IMPRINT",FACE,{"disambiguationData":[TD([[makeQuery(id+"F29.imprint","IMPRINT",EDGE,{"derivedFrom":sQuery(id+"F29.wireOp",EDGE,"E101")}),-1.0]])]});
            extrude(context, id + "F32", {"entities" : qUnion([Q0, Q1, Q2, Q3, Q4]), "operationType" : NewBodyOperationType.REMOVE, "oppositeDirection" : true, "depth" : 1 * mm});
        }
        {
            var Q0;
            Q0=makeQuery(id+"F30.boolean.opBoolean","COPY",EDGE,{"derivedFrom":makeQuery(id+"F30.opExtrude","CAP_EDGE",EDGE,{"disambiguationData":[OSD([sQuery(id+"F29.wireOp",EDGE,"E53")])],"isStart":false})});
            var Q1;
            Q1=makeQuery(id+"F30.boolean.opBoolean","COPY",EDGE,{"derivedFrom":makeQuery(id+"F30.opExtrude","CAP_EDGE",EDGE,{"disambiguationData":[OSD([sQuery(id+"F29.wireOp",EDGE,"E52")])],"isStart":false})});
            var Q2;
            Q2=makeQuery(id+"F30.boolean.opBoolean","COPY",EDGE,{"derivedFrom":makeQuery(id+"F30.opExtrude","CAP_EDGE",EDGE,{"disambiguationData":[OSD([sQuery(id+"F29.wireOp",EDGE,"E66")])],"isStart":false})});
            var Q3;
            Q3=makeQuery(id+"F30.boolean.opBoolean","COPY",EDGE,{"derivedFrom":makeQuery(id+"F30.opExtrude","CAP_EDGE",EDGE,{"disambiguationData":[OSD([sQuery(id+"F29.wireOp",EDGE,"E123")])],"isStart":false})});
            chamfer(context, id + "F33", {"entities" : qUnion([Q0, Q1, Q2, Q3]), "width" : 0.3 * mm, "tangentPropagation" : true});
        }
    });
